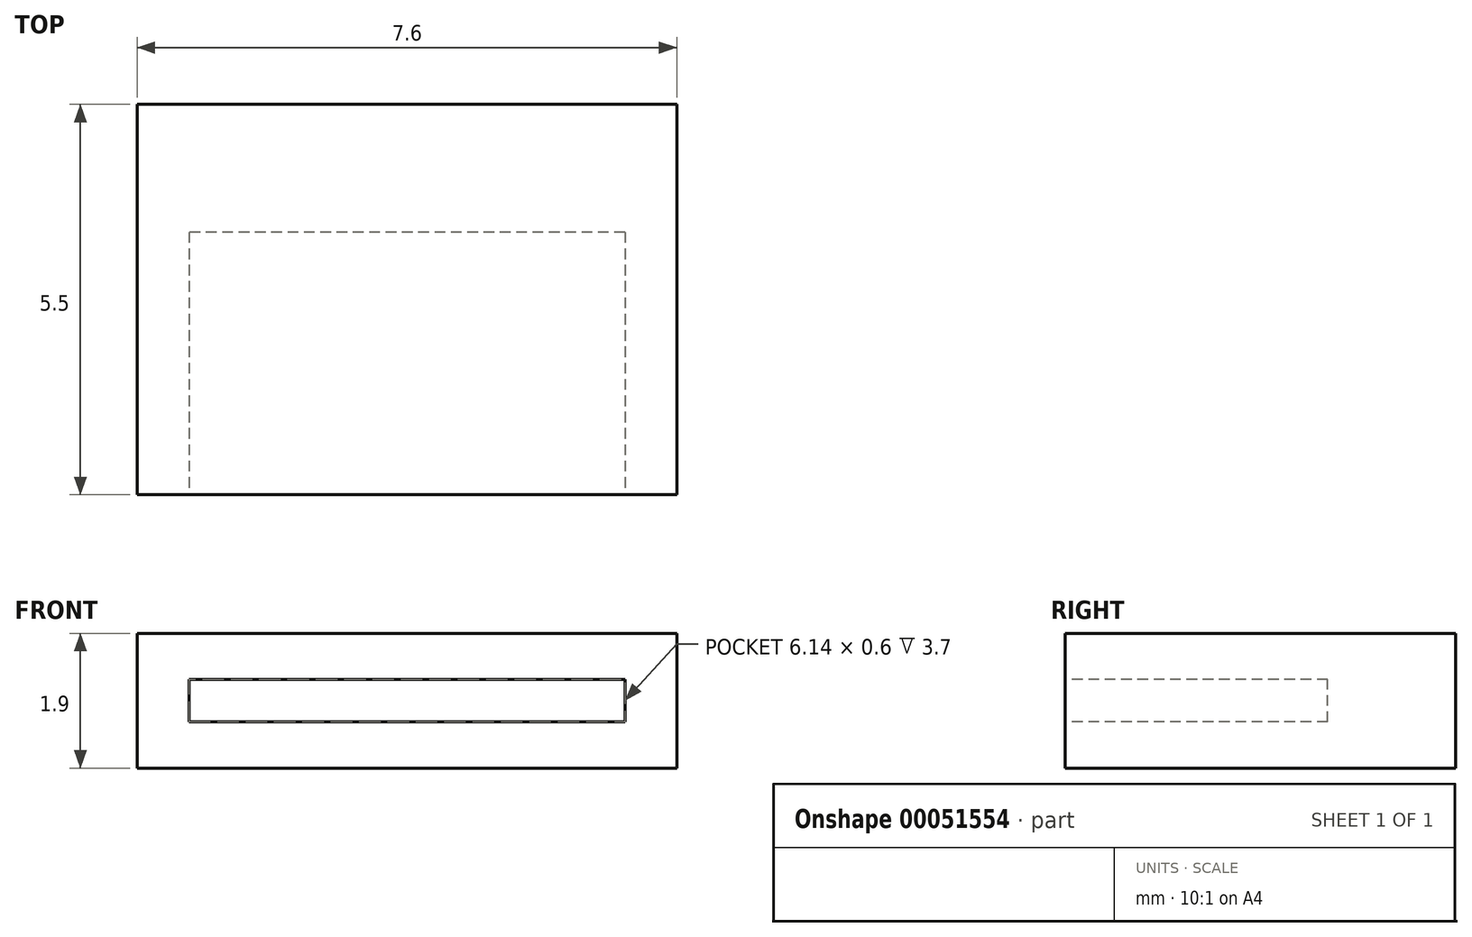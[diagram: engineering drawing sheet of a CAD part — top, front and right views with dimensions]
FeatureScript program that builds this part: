
annotation { "Feature Type Name" : "Feature", "Feature Type Description" : "" }
export const myFeature = defineFeature(function(context is Context, id is Id, definition is map)
    precondition{}
    {
        {
            var Q0;
            Q0=qCreatedBy(makeId("Top.planeOp"),FACE);
            var sketch = newSketch(context, id + "F0", { "sketchPlane" : qUnion([Q0])});
            skLineSegment(sketch, "E0.bottom", {"start": v(0, 0) * mm, "end": v(7.6, 0) * mm});
            skLineSegment(sketch, "E0.top", {"start": v(0, 5.5) * mm, "end": v(7.6, 5.5) * mm});
            skLineSegment(sketch, "E0.left", {"start": v(0, 0) * mm, "end": v(0, 5.5) * mm});
            skLineSegment(sketch, "E0.right", {"start": v(7.6, 0) * mm, "end": v(7.6, 5.5) * mm});
            skSolve(sketch);
        }
        {
            var Q0;
            Q0 = qSketchRegion(id + "F0", true);
            extrude(context, id + "F1", {"entities" : qUnion([Q0]), "depth" : 1.9 * mm});
        }
        {
            var Q0;
            Q0=makeQuery(id+"F1.opExtrude","SWEPT_FACE",FACE,{"disambiguationData":[OSD([sQuery(id+"F0.wireOp",EDGE,"E0.bottom")])]});
            var sketch = newSketch(context, id + "F2", { "sketchPlane" : qUnion([Q0])});
            skLineSegment(sketch, "E1.rect.bottom", {"start": v(6.87, 0.65) * mm, "end": v(0.73, 0.65) * mm});
            skLineSegment(sketch, "E1.rect.top", {"start": v(6.87, 1.25) * mm, "end": v(0.73, 1.25) * mm});
            skLineSegment(sketch, "E1.rect.left", {"start": v(6.87, 0.65) * mm, "end": v(6.87, 1.25) * mm});
            skLineSegment(sketch, "E1.rect.right", {"start": v(0.73, 0.65) * mm, "end": v(0.73, 1.25) * mm});
            skPoint(sketch, "E1.rect.middle", {"position": v(3.8, 0.95) * mm});
            skPoint(sketch, "E1.rect.middle.positionSnap0", {"position": v(3.8, 1.9) * mm});
            skPoint(sketch, "E1.rect.middle.positionSnap1", {"position": v(0, 0.95) * mm});
            skPoint(sketch, "E1.rect.centerSnap0", {"position": v(3.8, 1.9) * mm});
            skPoint(sketch, "E1.rect.centerSnap1", {"position": v(0, 0.95) * mm});
            skSolve(sketch);
        }
        {
            var Q0;
            Q0=makeQuery(id+"F2.imprint","IMPRINT",FACE,{"disambiguationData":[TD([[makeQuery(id+"F2.imprint","IMPRINT",EDGE,{"derivedFrom":sQuery(id+"F2.wireOp",EDGE,"E1.rect.bottom")}),-1.0]])]});
            extrude(context, id + "F3", {"entities" : qUnion([Q0]), "operationType" : NewBodyOperationType.REMOVE, "oppositeDirection" : true, "depth" : 3.7 * mm});
        }
    });
